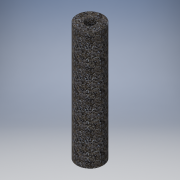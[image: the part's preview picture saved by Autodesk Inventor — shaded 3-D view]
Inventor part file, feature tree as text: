
AUTODESK INVENTOR PART (.ipt)
format: ipt  version: 2019 (Build 230136000, 136)  size: 110,592 bytes
history: native  units: in
note: dims shown in document units (in); Inventor stores cm internally (conversion verified against a paired STEP export)
features: extrude x1, sketch x1
ambient origin geometry x8: Origin, YZ Plane, XZ Plane, XY Plane, X Axis, Y Axis, Z Axis, Center Point
bodies: Solid1 (feature_tree)
feature tree (2):
  extrude  "Extrusion1"  Depth=39.3701in
  sketch  "Sketch1"  dims[d0=3.1496in d1=8.6614in d2=39.3701in d3=0.0in]
